# Revit family: AFX_Inc-Duncan-20_In-Ceiling_Light-
name_source: partatom
category: Lighting Fixtures
revit_build: Autodesk Revit 2016 (Build: 20150220_1215(x64)
units: mm (PartAtom-declared; Revit-internal decimal feet)

## family parameters
Cut with Voids When Loaded = No
Host = Face
Light Source = Yes
Part Type = Normal
Room Calculation Point = No
Round Connector Dimension = Use Diameter
Shared = No

## types (2) — shared parameters
Apparent Load = 0 VA
Assembly Code = E1020300
Body Finish = AFX - Metal Powder Coated Black
Bulb Category = LED
Color Filter = 16777215
Color Rendering Index = 90
Default Elevation = 48"
Depth = 4 15/16"
Diameter = 20"
Diffuser Finish = AFX - Diffuser Frosted
Dimming Lamp Color Temperature Shift = <None>
Emit Shape Visible in Rendering = Yes
Emit from Circle Diameter = 19"
Keynote = 12500
Lamp = LED
Manufacturer = AFX Inc
Product Documentation Link = https://www.afx.lightingnewyork.com
Revit Model Built By = https://servex-us.com
Tilt Angle = 90.00°
Total Lumens = 4000
Total Wattage = 40 W
Type Comments = Watson
URL = www.afxinc.com
Voltage = 120 V
Wattage Comments = 1 x 40W Integrated LED

## per-type parameters (varying)
| type | Description | Photometric Web File | Shade Finish |
| DUNF - 20DUNF20LAJUDBKGD | Duncan 1 Light 20 inch Black and Gold Flush Mount Ceiling Light | DUNF - 20DUNF20LAJUDBKGD.IES | AFX - Shade White |
| DUNF - 20DUNF20LAJUDBKWH | Duncan 1 Light 20 inch Black and White Flush Mount Ceiling Light | DUNF - 20DUNF20LAJUDBKWH.IES | AFX - Shade Gold |

note: column(s) folded — value = type name in every type: Model

## geometry (parser evidence)
native form markers: Sweep x3
no freeform markers — native parametric forms only
